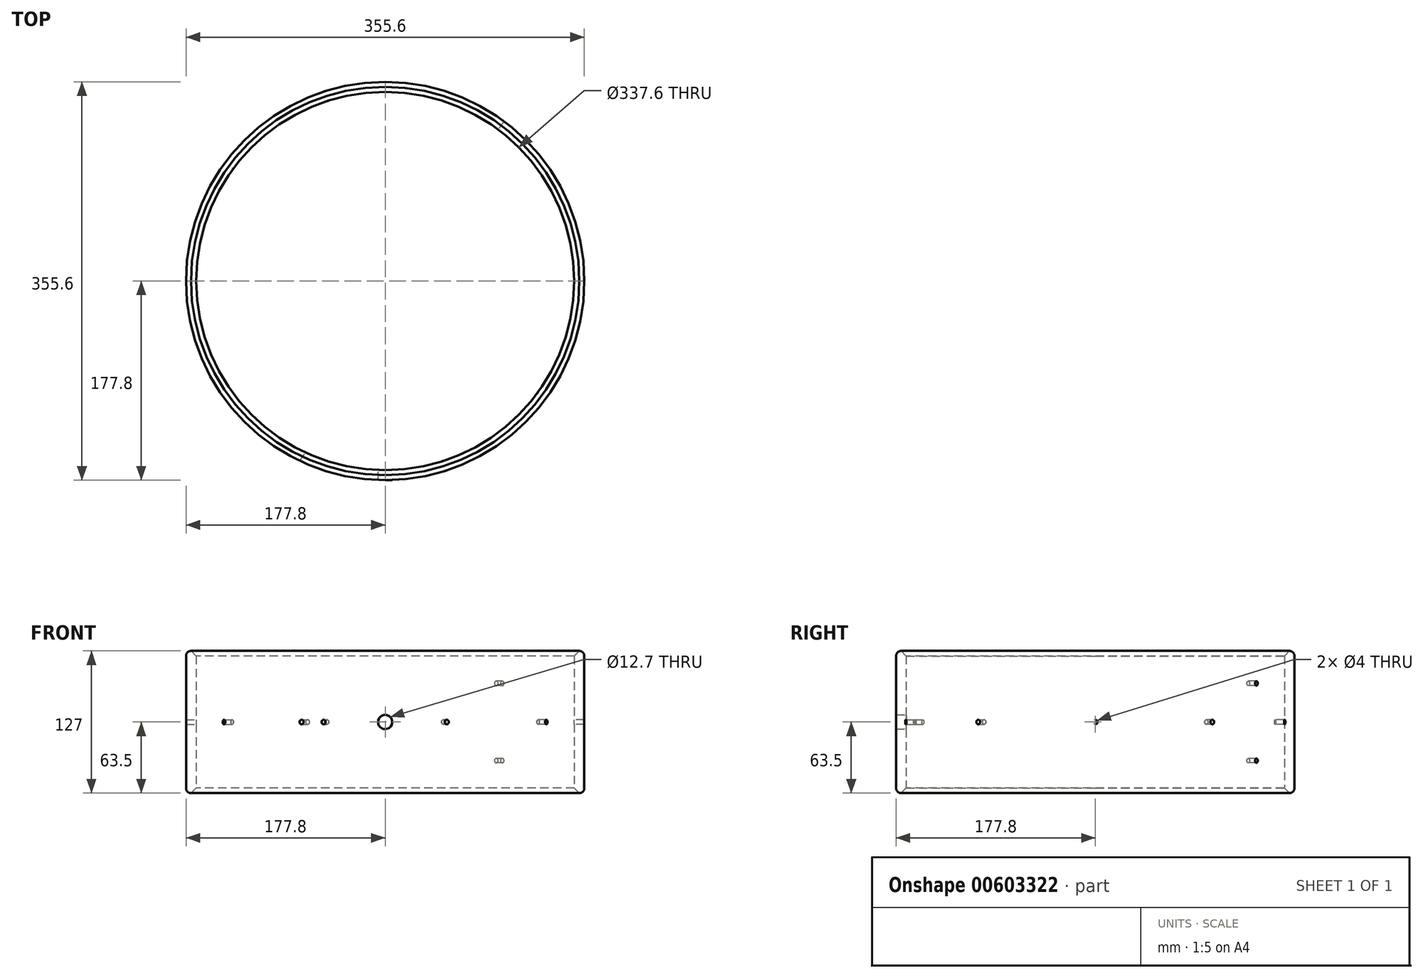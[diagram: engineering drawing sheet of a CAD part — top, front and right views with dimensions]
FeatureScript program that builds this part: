
annotation { "Feature Type Name" : "Feature", "Feature Type Description" : "" }
export const myFeature = defineFeature(function(context is Context, id is Id, definition is map)
    precondition{}
    {
        {
            var Q0;
            Q0=qCreatedBy(makeId("Top.planeOp"),FACE);
            var sketch = newSketch(context, id + "F0", { "sketchPlane" : qUnion([Q0])});
            skCircle(sketch, "E0", {"center": v(0, 0) * mm, "radius": 177.8 * mm});
            skCircle(sketch, "E1.0", {"center": v(0, 0) * mm, "radius": 168.8 * mm});
            skCircle(sketch, "E2.0", {"center": v(0, 0) * mm, "radius": 173.3 * mm});
            skLineSegment(sketch, "E3", {"start": v(0, 0) * mm, "end": v(0, 92.05) * mm, "construction": true});
            skLineSegment(sketch, "E4.bottom", {"start": v(0, 0) * mm, "end": v(-60.16, 0) * mm, "construction": true});
            skLineSegment(sketch, "E4.top", {"start": v(0, 67.16) * mm, "end": v(-60.16, 67.16) * mm, "construction": true});
            skLineSegment(sketch, "E4.left", {"start": v(0, 0) * mm, "end": v(0, 67.16) * mm, "construction": true});
            skLineSegment(sketch, "E4.right", {"start": v(-60.16, 0) * mm, "end": v(-60.16, 67.16) * mm, "construction": true});
            skSolve(sketch);
        }
        {
            var Q0;
            Q0=makeQuery(id+"F0.imprint","IMPRINT",FACE,{"disambiguationData":[TD([[makeQuery(id+"F0.imprint","IMPRINT",EDGE,{"derivedFrom":sQuery(id+"F0.wireOp",EDGE,"E0")}),1.0]])]});
            var Q1;
            Q1=makeQuery(id+"F0.imprint","IMPRINT",FACE,{"disambiguationData":[TD([[makeQuery(id+"F0.imprint","IMPRINT",EDGE,{"derivedFrom":sQuery(id+"F0.wireOp",EDGE,"E1.0")}),-1.0]])]});
            extrude(context, id + "F1", {"entities" : qUnion([Q0, Q1]), "depth" : 127 * mm, "offsetDistance" : 25.4 * mm});
        }
        {
            var Q0;
            Q0=makeQuery(id+"F1.opExtrude","CAP_EDGE",EDGE,{"disambiguationData":[OSD([sQuery(id+"F0.wireOp",EDGE,"E1.0")])],"isStart":true});
            chamfer(context, id + "F2", {"entities" : qUnion([Q0]), "width" : 4.5 * mm, "tangentPropagation" : true});
        }
        {
            var Q0;
            Q0=makeQuery(id+"F1.opExtrude","CAP_EDGE",EDGE,{"disambiguationData":[OSD([sQuery(id+"F0.wireOp",EDGE,"E0")])],"isStart":true});
            fillet(context, id + "F3", {"entities" : qUnion([Q0]), "radius" : 4.5 * mm, "tangentPropagation" : true, "allowEdgeOverflow" : false});
        }
        {
            var Q0;
            Q0=makeQuery(id+"F1.opExtrude","CAP_EDGE",EDGE,{"disambiguationData":[OSD([sQuery(id+"F0.wireOp",EDGE,"E1.0")])],"isStart":false});
            chamfer(context, id + "F4", {"entities" : qUnion([Q0]), "width" : 4.5 * mm, "tangentPropagation" : true});
        }
        {
            var Q0;
            Q0=makeQuery(id+"F1.opExtrude","CAP_EDGE",EDGE,{"disambiguationData":[OSD([sQuery(id+"F0.wireOp",EDGE,"E0")])],"isStart":false});
            fillet(context, id + "F5", {"entities" : qUnion([Q0]), "radius" : 4.5 * mm, "tangentPropagation" : true, "allowEdgeOverflow" : false});
        }
        {
            var Q0;
            Q0=makeQuery(id+"F1.opExtrude","SWEPT_FACE",FACE,{"disambiguationData":[OSD([sQuery(id+"F0.wireOp",EDGE,"E0")])]});
            cPlane(context, id + "F6", {"entities" : qUnion([Q0]), "cplaneType" : CPlaneType.LINE_ANGLE, "offset" : 25.4 * mm, "angle" : 0 * degree, "width" : 152.4 * mm, "height" : 152.4 * mm});
        }
        {
            var Q0;
            Q0=qCreatedBy(id+"F6.planeOp",FACE);
            var sketch = newSketch(context, id + "F7", { "sketchPlane" : qUnion([Q0])});
            skPoint(sketch, "E5", {"position": v(0, 63.5) * mm});
            skCircle(sketch, "E6", {"center": v(0, 63.5) * mm, "radius": 2 * mm});
            skLineSegment(sketch, "E7", {"start": v(0, 63.5) * mm, "end": v(0, 111.1) * mm, "construction": true});
            skSolve(sketch);
        }
        {
            var Q0;
            Q0=makeQuery(id+"F7.imprint","IMPRINT",FACE,{"disambiguationData":[TD([[makeQuery(id+"F7.imprint","IMPRINT",EDGE,{"derivedFrom":sQuery(id+"F7.wireOp",EDGE,"DPJ1Udg9-G2gh-IGET-F7KI-FzSwoKrtSLhG")}),1.0]])]});
            var Q1;
            Q1=makeQuery(id+"F7.imprint","IMPRINT",FACE,{"disambiguationData":[TD([[makeQuery(id+"F7.imprint","IMPRINT",EDGE,{"derivedFrom":sQuery(id+"F7.wireOp",EDGE,"bZP9mFup-iXVF-BwQI-PD0N-axWwuiav8JT6")}),1.0]])]});
            var Q2;
            Q2=makeQuery(id+"F7.imprint","IMPRINT",FACE,{"disambiguationData":[TD([[makeQuery(id+"F7.imprint","IMPRINT",EDGE,{"derivedFrom":sQuery(id+"F7.wireOp",EDGE,"E6")}),1.0]])]});
            extrude(context, id + "F8", {"entities" : qUnion([Q0, Q1, Q2]), "operationType" : NewBodyOperationType.REMOVE, "depth" : 222.5 * mm, "offsetDistance" : 25.4 * mm});
        }
        {
            var Q0;
            Q0=makeQuery(id+"F8.boolean.opBoolean","COPY",FACE,{"derivedFrom":makeQuery(id+"F8.opExtrude","SWEPT_FACE",FACE,{"disambiguationData":[OSD([sQuery(id+"F7.wireOp",EDGE,"E6")])]})});
            var Q1;
            Q1=sQuery(id+"F7.wireOp",EDGE,"E7");
            circularPattern(context, id + "F9", {"patternType" : PatternType.FACE, "operationType" : NewBodyOperationType.REMOVE, "faces" : qUnion([Q0]), "axis" : qUnion([Q1]), "angle" : 360 * degree, "instanceCount" : 10, "equalSpace" : true});
        }
        {
            var Q0;
            Q0=qCreatedBy(id+"F6.planeOp",FACE);
            var Q1;
            Q1=sQuery(id+"F7.wireOp",EDGE,"E7");
            cPlane(context, id + "F10", {"entities" : qUnion([Q0, Q1]), "cplaneType" : CPlaneType.LINE_ANGLE, "offset" : 25.4 * mm, "angle" : 90 * degree, "width" : 152.4 * mm, "height" : 152.4 * mm});
        }
        {
            var Q0;
            Q0=qCreatedBy(id+"F10.planeOp",FACE);
            var sketch = newSketch(context, id + "F11", { "sketchPlane" : qUnion([Q0])});
            skPoint(sketch, "E8", {"position": v(0, 63.5) * mm});
            skCircle(sketch, "E9", {"center": v(0, 63.5) * mm, "radius": 6.35 * mm});
            skSolve(sketch);
        }
        {
            var Q0;
            Q0 = qSketchRegion(id + "F11", true);
            extrude(context, id + "F12", {"entities" : qUnion([Q0]), "operationType" : NewBodyOperationType.REMOVE, "oppositeDirection" : true, "depth" : 251.97 * mm, "offsetDistance" : 25.4 * mm});
        }
        {
            var Q0;
            Q0=qCreatedBy(id+"F10.planeOp",FACE);
            var Q1;
            Q1=sQuery(id+"F7.wireOp",EDGE,"E7");
            cPlane(context, id + "F13", {"entities" : qUnion([Q0, Q1]), "cplaneType" : CPlaneType.LINE_ANGLE, "offset" : 25.4 * mm, "angle" : 36 * degree, "oppositeDirection" : true, "width" : 152.4 * mm, "height" : 152.4 * mm});
        }
        {
            var Q0;
            Q0=qCreatedBy(id+"F13.planeOp",FACE);
            var sketch = newSketch(context, id + "F14", { "sketchPlane" : qUnion([Q0])});
            skPoint(sketch, "E10", {"position": v(0, 63.5) * mm});
            skLineSegment(sketch, "E11", {"start": v(0, 63.5) * mm, "end": v(0, 88.5) * mm, "construction": true});
            skLineSegment(sketch, "E12", {"start": v(0, 63.5) * mm, "end": v(34.5, 63.5) * mm, "construction": true});
            skCircle(sketch, "E13", {"center": v(34.5, 63.5) * mm, "radius": 2 * mm});
            skCircle(sketch, "E14", {"center": v(0, 63.5) * mm, "radius": 2 * mm});
            skLineSegment(sketch, "E15", {"start": v(0, 63.5) * mm, "end": v(0, 98) * mm, "construction": true});
            skLineSegment(sketch, "E16", {"start": v(0, 63.5) * mm, "end": v(0, 28.98) * mm, "construction": true});
            skCircle(sketch, "E17", {"center": v(0, 98) * mm, "radius": 2 * mm});
            skCircle(sketch, "E18", {"center": v(0, 28.98) * mm, "radius": 2 * mm});
            skCircle(sketch, "E19.MirrorC", {"center": v(-34.5, 63.5) * mm, "radius": 2 * mm});
            skLineSegment(sketch, "E20.MirrorCS", {"start": v(0, 63.5) * mm, "end": v(-34.5, 63.5) * mm, "construction": true});
            skSolve(sketch);
        }
        {
            var Q0;
            Q0=makeQuery(id+"F14.imprint","IMPRINT",FACE,{"disambiguationData":[TD([[makeQuery(id+"F14.imprint","IMPRINT",EDGE,{"derivedFrom":sQuery(id+"F14.wireOp",EDGE,"E19.MirrorC")}),-1.0]])]});
            var Q1;
            Q1=makeQuery(id+"F14.imprint","IMPRINT",FACE,{"disambiguationData":[TD([[makeQuery(id+"F14.imprint","IMPRINT",EDGE,{"derivedFrom":sQuery(id+"F14.wireOp",EDGE,"E13")}),1.0]])]});
            extrude(context, id + "F15", {"entities" : qUnion([Q0, Q1]), "operationType" : NewBodyOperationType.REMOVE, "depth" : 370.84 * mm, "offsetDistance" : 25.4 * mm});
        }
        {
            var Q0;
            Q0=makeQuery(id+"F14.imprint","IMPRINT",FACE,{"disambiguationData":[TD([[makeQuery(id+"F14.imprint","IMPRINT",EDGE,{"derivedFrom":sQuery(id+"F14.wireOp",EDGE,"E17")}),1.0]])]});
            var Q1;
            Q1=makeQuery(id+"F14.imprint","IMPRINT",FACE,{"disambiguationData":[TD([[makeQuery(id+"F14.imprint","IMPRINT",EDGE,{"derivedFrom":sQuery(id+"F14.wireOp",EDGE,"E18")}),1.0]])]});
            extrude(context, id + "F16", {"entities" : qUnion([Q0, Q1]), "operationType" : NewBodyOperationType.REMOVE, "oppositeDirection" : true, "depth" : 188.72 * mm, "offsetDistance" : 25.4 * mm});
        }
        {
            var Q0;
            Q0=makeQuery(id+"F0.imprint","IMPRINT",FACE,{"disambiguationData":[TD([[makeQuery(id+"F0.imprint","IMPRINT",EDGE,{"derivedFrom":sQuery(id+"F0.wireOp",EDGE,"E1.0")}),1.0]])]});
            cPlane(context, id + "F17", {"entities" : qUnion([Q0]), "cplaneType" : CPlaneType.OFFSET, "offset" : 127 * mm, "width" : 152.4 * mm, "height" : 152.4 * mm});
        }
    });
